FCSTD DOCUMENT  (FreeCAD 0.22R37100 (Git))
Label: composit_stand12_model
License: All rights reserved
LicenseURL: http://en.wikipedia.org/wiki/All_rights_reserved
objects: App::Link×29, App::DocumentObjectGroup×2, PartDesign::CoordinateSystem×1, App::Part×1, Measure::MeasureDistance×1
note: 1 computed .brp shape members not serialized (recipe doc carries the construction recipe); baked Part::Feature solids carry a one-line shape summary decoded from their .brp
EXTERNAL_REF file=composit_stand12.FCStd obj=Local_CS005
EXTERNAL_REF file=composit_stand12.FCStd obj=Body
EXTERNAL_REF file=composit_stand12.FCStd obj=Local_CS004
EXTERNAL_REF file=composit_stand12.FCStd obj=Local_CS006
EXTERNAL_REF file=composit_stand12.FCStd obj=Body002
EXTERNAL_REF file=composit_stand12.FCStd obj=LCS_1
EXTERNAL_REF file=composit_stand12.FCStd obj=Part
EXTERNAL_REF file=composit_stand12.FCStd obj=Local_CS002
EXTERNAL_REF file=composit_stand12.FCStd obj=Local_CS007
EXTERNAL_REF file=composit_stand12.FCStd obj=Body004
EXTERNAL_REF file=composit_stand12.FCStd obj=Local_CS016
EXTERNAL_REF file=composit_stand12.FCStd obj=Local_CS042
EXTERNAL_REF file=composit_stand12.FCStd obj=Body009
EXTERNAL_REF file=composit_stand12.FCStd obj=Local_CS008
EXTERNAL_REF file=composit_stand12.FCStd obj=Local_CS012
EXTERNAL_REF file=composit_stand12.FCStd obj=Body006
EXTERNAL_REF file=composit_stand12.FCStd obj=Local_CS009
EXTERNAL_REF file=composit_stand12.FCStd obj=Local_CS013
EXTERNAL_REF file=composit_stand12.FCStd obj=Body008
EXTERNAL_REF file=composit_stand12.FCStd obj=Local_CS010
EXTERNAL_REF file=composit_stand12.FCStd obj=Local_CS011
EXTERNAL_REF file=composit_stand12.FCStd obj=Local_CS017
EXTERNAL_REF file=composit_stand12.FCStd obj=Local_CS019
EXTERNAL_REF file=composit_stand12.FCStd obj=Body010
EXTERNAL_REF file=composit_stand12.FCStd obj=Local_CS018
EXTERNAL_REF file=composit_stand12.FCStd obj=Body012
EXTERNAL_REF file=../composit_electric_shield.FCStd obj=Local_CS
EXTERNAL_REF file=composit_stand12.FCStd obj=Local_CS020
EXTERNAL_REF file=../composit_electric_shield.FCStd obj=Body
EXTERNAL_REF file=composit_stand12.FCStd obj=Local_CS014
EXTERNAL_REF file=../rails.FCStd obj=LCS_1
EXTERNAL_REF file=../rails.FCStd obj=Part
EXTERNAL_REF file=composit_stand12.FCStd obj=Local_CS015
EXTERNAL_REF file=../basin450x225x125.FCStd obj=Local_CS
EXTERNAL_REF file=composit_stand12.FCStd obj=Local_CS023
EXTERNAL_REF file=../basin450x225x125.FCStd obj=Body
EXTERNAL_REF file=../basin450x225x125.FCStd obj=Local_CS001
EXTERNAL_REF file=../basin450x225x125.FCStd obj=Body001
EXTERNAL_REF file=composit_stand12.FCStd obj=Local_CS024
EXTERNAL_REF file=composit_stand12.FCStd obj=Body015
EXTERNAL_REF file=composit_stand12.FCStd obj=Local_CS025
EXTERNAL_REF file=composit_stand12.FCStd obj=Body016
EXTERNAL_REF file=composit_stand12.FCStd obj=Local_CS027
EXTERNAL_REF file=composit_stand12.FCStd obj=Local_CS028
EXTERNAL_REF file=composit_stand12.FCStd obj=Body018
EXTERNAL_REF file=composit_stand12.FCStd obj=Local_CS029
EXTERNAL_REF file=composit_stand12.FCStd obj=Local_CS030
EXTERNAL_REF file=composit_stand12.FCStd obj=Body019
EXTERNAL_REF file=composit_stand12.FCStd obj=Local_CS001
EXTERNAL_REF file=composit_stand12.FCStd obj=Local_CS003
EXTERNAL_REF file=composit_stand12.FCStd obj=Body005
EXTERNAL_REF file=composit_stand12.FCStd obj=Local_CS031
EXTERNAL_REF file=composit_stand12.FCStd obj=Local_CS032
EXTERNAL_REF file=composit_stand12.FCStd obj=Local_CS033
EXTERNAL_REF file=composit_stand12.FCStd obj=Local_CS034
EXTERNAL_REF file=composit_stand12.FCStd obj=Body022
EXTERNAL_REF file=composit_stand12.FCStd obj=Local_CS035
EXTERNAL_REF file=composit_stand12.FCStd obj=Local_CS036
EXTERNAL_REF file=composit_stand12.FCStd obj=Body023
EXTERNAL_REF file=composit_stand12.FCStd obj=Local_CS040
EXTERNAL_REF file=composit_stand12.FCStd obj=Body025
EXTERNAL_REF file=composit_stand12.FCStd obj=Local_CS039
EXTERNAL_REF file=composit_stand12.FCStd obj=Local_CS041
EXTERNAL_REF file=composit_stand12.FCStd obj=Body026

FEATURE [App::DocumentObjectGroup] Parts
FEATURE [PartDesign::CoordinateSystem] LCS_Origin
  AttacherType = Attacher::AttachEngine3D
  AttachmentOffset = pos=(0,0,0) rot=(0,0,1;3.14159rad)
  AttachmentSupport = -> [XY_Plane]
  MapMode = 5
  Placement = pos=(0,0,0) rot=(0,0,1;3.14159rad)
FEATURE [App::Link] face
  AttachedBy = #Local_CS005
  AttachedTo = Parent Assembly#LCS_Origin
  LinkPlacement = pos=(0,0,0) rot=(0,0,1;3.14159rad)
  LinkedObject = -> <external composit_stand12.FCStd>#Body
  Placement = pos=(0,0,0) rot=(0,0,1;3.14159rad)
  SolverId = Asm4EE
  expr: Placement = LCS_Origin.Placement * AttachmentOffset * composit_stand12#Local_CS005.Placement ^ -1
FEATURE [App::Link] sink
  AttachedBy = #Local_CS004
  AttachedTo = face#Local_CS006
  LinkPlacement = pos=(-3.7e-15,-30,148) rot=(0,0,1;3.14159rad)
  LinkedObject = -> <external composit_stand12.FCStd>#Body002
  Placement = pos=(-3.7e-15,-30,148) rot=(0,0,1;3.14159rad)
  SolverId = Asm4EE
  expr: Placement = face.Placement * composit_stand12#Local_CS006.Placement * AttachmentOffset * composit_stand12#Local_CS004.Placement ^ -1
FEATURE [App::Link] modules
  AttachedBy = #LCS_1
  AttachedTo = face#Local_CS005
  LinkPlacement = pos=(0,0,0) rot=(0,0,1;3.14159rad)
  LinkedObject = -> <external composit_stand12.FCStd>#Part
  Placement = pos=(0,0,0) rot=(0,0,1;3.14159rad)
  SolverId = Asm4EE
  expr: Placement = face.Placement * composit_stand12#Local_CS005.Placement * AttachmentOffset * composit_stand12#LCS_1.Placement ^ -1
FEATURE [App::Link] dropper_fix_composit
  AttachedBy = #Local_CS002
  AttachedTo = face#Local_CS007
  LinkPlacement = pos=(-3.7e-15,-30,1163.4) rot=(0,0,1;3.14159rad)
  LinkedObject = -> <external composit_stand12.FCStd>#Body004
  Placement = pos=(-3.7e-15,-30,1163.4) rot=(0,0,1;3.14159rad)
  SolverId = Asm4EE
  expr: Placement = face.Placement * composit_stand12#Local_CS007.Placement * AttachmentOffset * composit_stand12#Local_CS002.Placement ^ -1
FEATURE [App::Link] pan
  AttachedBy = #Local_CS016
  AttachedTo = face#Local_CS042
  LinkPlacement = pos=(-1.2e-15,-10,10) rot=(0,0,1;3.14159rad)
  LinkedObject = -> <external composit_stand12.FCStd>#Body009
  Placement = pos=(-1.2e-15,-10,10) rot=(0,0,1;3.14159rad)
  SolverId = Asm4EE
  expr: Placement = face.Placement * composit_stand12#Local_CS042.Placement * AttachmentOffset * composit_stand12#Local_CS016.Placement ^ -1
FEATURE [App::Link] bar001
  AttachedBy = #Local_CS008
  AttachedTo = face#Local_CS012
  LinkPlacement = pos=(-3.3e-15,-27,958.5) rot=(0,1,0;1.5708rad)
  LinkedObject = -> <external composit_stand12.FCStd>#Body006
  Placement = pos=(-3.3e-15,-27,958.5) rot=(0,1,0;1.5708rad)
  SolverId = Asm4EE
  expr: Placement = face.Placement * composit_stand12#Local_CS012.Placement * AttachmentOffset * composit_stand12#Local_CS008.Placement ^ -1
FEATURE [App::Link] bar_fix
  AttachedBy = #Local_CS013
  AttachedTo = bar002#Local_CS009
  LinkPlacement = pos=(-444.137,-2,278.5) rot=(0.707107,0,0.707107;3.14159rad)
  LinkedObject = -> <external composit_stand12.FCStd>#Body008
  Placement = pos=(-444.137,-2,278.5) rot=(0.707107,0,0.707107;3.14159rad)
  SolverId = Asm4EE
  expr: Placement = bar002.Placement * composit_stand12#Local_CS009.Placement * AttachmentOffset * composit_stand12#Local_CS013.Placement ^ -1
FEATURE [App::Link] bar_fix001
  AttachedBy = #Local_CS013
  AttachedTo = bar002#Local_CS010
  LinkPlacement = pos=(444.137,-2,278.5) rot=(0.707107,0,-0.707107;3.14159rad)
  LinkedObject = -> <external composit_stand12.FCStd>#Body008
  Placement = pos=(444.137,-2,278.5) rot=(0.707107,0,-0.707107;3.14159rad)
  SolverId = Asm4EE
  expr: Placement = bar002.Placement * composit_stand12#Local_CS010.Placement * AttachmentOffset * composit_stand12#Local_CS013.Placement ^ -1
FEATURE [App::Link] bar_fix002
  AttachedBy = #Local_CS013
  AttachedTo = bar001#Local_CS009
  LinkPlacement = pos=(-444.137,-2,958.5) rot=(0.707107,0,0.707107;3.14159rad)
  LinkedObject = -> <external composit_stand12.FCStd>#Body008
  Placement = pos=(-444.137,-2,958.5) rot=(0.707107,0,0.707107;3.14159rad)
  SolverId = Asm4EE
  expr: Placement = bar001.Placement * composit_stand12#Local_CS009.Placement * AttachmentOffset * composit_stand12#Local_CS013.Placement ^ -1
FEATURE [App::Link] bar_fix003
  AttachedBy = #Local_CS013
  AttachedTo = bar001#Local_CS010
  LinkPlacement = pos=(444.137,-2,958.5) rot=(0.707107,0,-0.707107;3.14159rad)
  LinkedObject = -> <external composit_stand12.FCStd>#Body008
  Placement = pos=(444.137,-2,958.5) rot=(0.707107,0,-0.707107;3.14159rad)
  SolverId = Asm4EE
  expr: Placement = bar001.Placement * composit_stand12#Local_CS010.Placement * AttachmentOffset * composit_stand12#Local_CS013.Placement ^ -1
FEATURE [App::Link] bar002
  AttachedBy = #Local_CS008
  AttachedTo = face#Local_CS011
  LinkPlacement = pos=(-3.3e-15,-27,278.5) rot=(0,1,0;1.5708rad)
  LinkedObject = -> <external composit_stand12.FCStd>#Body006
  Placement = pos=(-3.3e-15,-27,278.5) rot=(0,1,0;1.5708rad)
  SolverId = Asm4EE
  expr: Placement = face.Placement * composit_stand12#Local_CS011.Placement * AttachmentOffset * composit_stand12#Local_CS008.Placement ^ -1
FEATURE [App::Link] cap_outer
  AttachedBy = #Local_CS017
  AttachedTo = face#Local_CS019
  LinkPlacement = pos=(0,0,1163.4) rot=(0,0,1;3.14159rad)
  LinkedObject = -> <external composit_stand12.FCStd>#Body010
  Placement = pos=(0,0,1163.4) rot=(0,0,1;3.14159rad)
  SolverId = Asm4EE
  expr: Placement = face.Placement * composit_stand12#Local_CS019.Placement * AttachmentOffset * composit_stand12#Local_CS017.Placement ^ -1
FEATURE [App::Link] cap_inner
  AttachedBy = #Local_CS018
  AttachedTo = cap_outer#Local_CS017
  LinkPlacement = pos=(0,0,1163.4) rot=(0,0,1;3.14159rad)
  LinkedObject = -> <external composit_stand12.FCStd>#Body012
  Placement = pos=(0,0,1163.4) rot=(0,0,1;3.14159rad)
  SolverId = Asm4EE
  expr: Placement = cap_outer.Placement * composit_stand12#Local_CS017.Placement * AttachmentOffset * composit_stand12#Local_CS018.Placement ^ -1
FEATURE [App::Link] composit_electric_shield_inner
  AttachedBy = #Local_CS
  AttachedTo = face#Local_CS020
  LinkPlacement = pos=(-413.737,-125,930) rot=(-0.57735,0.57735,0.57735;4.18879rad)
  LinkedObject = -> <external ../composit_electric_shield.FCStd>#Body
  Placement = pos=(-413.737,-125,930) rot=(-0.57735,0.57735,0.57735;4.18879rad)
  SolverId = Asm4EE
  expr: Placement = face.Placement * composit_stand12#Local_CS020.Placement * AttachmentOffset * composit_electric_shield#Local_CS.Placement ^ -1
FEATURE [App::Link] rail_Part
  AttachedBy = #LCS_1
  AttachedTo = face#Local_CS014
  LinkPlacement = pos=(-441.137,-4,23) rot=(0.707107,0,0.707107;3.14159rad)
  LinkedObject = -> <external ../rails.FCStd>#Part
  Placement = pos=(-441.137,-4,23) rot=(0.707107,0,0.707107;3.14159rad)
  SolverId = Asm4EE
  expr: Placement = face.Placement * composit_stand12#Local_CS014.Placement * AttachmentOffset * rails#LCS_1.Placement ^ -1
FEATURE [App::Link] rail_Part001
  AttachedBy = #LCS_1
  AttachedTo = face#Local_CS015
  LinkPlacement = pos=(441.137,-4,23) rot=(-0.707107,0,0.707107;3.14159rad)
  LinkedObject = -> <external ../rails.FCStd>#Part
  Placement = pos=(441.137,-4,23) rot=(-0.707107,0,0.707107;3.14159rad)
  SolverId = Asm4EE
  expr: Placement = face.Placement * composit_stand12#Local_CS015.Placement * AttachmentOffset * rails#LCS_1.Placement ^ -1
FEATURE [App::Link] basin450x225x125
  AttachedBy = #Local_CS
  AttachedTo = pan#Local_CS023
  AttachmentOffset = pos=(0,0,0) rot=(0,0,1;3.14159rad)
  LinkPlacement = pos=(-1.59e-14,-130,13) rot=(0,0,1;0rad)
  LinkedObject = -> <external ../basin450x225x125.FCStd>#Body
  Placement = pos=(-1.59e-14,-130,13) rot=(0,0,1;0rad)
  SolverId = Asm4EE
  expr: Placement = pan.Placement * composit_stand12#Local_CS023.Placement * AttachmentOffset * basin450x225x125#Local_CS.Placement ^ -1
FEATURE [App::Link] basin450x225x125_pump_holder
  AttachedBy = #Local_CS001
  AttachedTo = basin450x225x125#Local_CS
  LinkPlacement = pos=(-1.59e-14,-130,13) rot=(0,0,1;0rad)
  LinkedObject = -> <external ../basin450x225x125.FCStd>#Body001
  Placement = pos=(-1.59e-14,-130,13) rot=(0,0,1;0rad)
  SolverId = Asm4EE
  expr: Placement = basin450x225x125.Placement * basin450x225x125#Local_CS.Placement * AttachmentOffset * basin450x225x125#Local_CS001.Placement ^ -1
FEATURE [App::Link] basin_fix
  AttachedBy = #Local_CS024
  AttachedTo = pan#Local_CS016
  LinkPlacement = pos=(-1.2e-15,-10,13) rot=(0,0,1;3.14159rad)
  LinkedObject = -> <external composit_stand12.FCStd>#Body015
  Placement = pos=(-1.2e-15,-10,13) rot=(0,0,1;3.14159rad)
  SolverId = Asm4EE
  expr: Placement = pan.Placement * composit_stand12#Local_CS016.Placement * AttachmentOffset * composit_stand12#Local_CS024.Placement ^ -1
FEATURE [App::Link] door_plexiglass
  AttachedBy = #Local_CS025
  AttachedTo = door_ss#Local_CS026
  LinkPlacement = pos=(3.979e-13,-315.383,250) rot=(0,0,1;3.14159rad)
  LinkedObject = -> <external composit_stand12.FCStd>#Body016
  Placement = pos=(3.979e-13,-315.383,250) rot=(0,0,1;3.14159rad)
  SolverId = Asm4EE
  expr: Placement = door_ss.Placement * composit_stand12#Local_CS026.Placement * AttachmentOffset * composit_stand12#Local_CS025.Placement ^ -1
FEATURE [App::Link] sink_cutout
  AttachedBy = #Local_CS028
  AttachedTo = sink#Local_CS027
  LinkPlacement = pos=(-1.45e-14,-118.451,164.625) rot=(0,0.09276,0.995689;3.14159rad)
  LinkedObject = -> <external composit_stand12.FCStd>#Body018
  Placement = pos=(-1.45e-14,-118.451,164.625) rot=(0,0.09276,0.995689;3.14159rad)
  SolverId = Asm4EE
  expr: Placement = sink.Placement * composit_stand12#Local_CS027.Placement * AttachmentOffset * composit_stand12#Local_CS028.Placement ^ -1
FEATURE [App::Link] sink_jumb
  AttachedBy = #Local_CS030
  AttachedTo = sink#Local_CS029
  LinkPlacement = pos=(-2.56e-14,-216.86,182.409) rot=(1,0,0;6.0974rad)
  LinkedObject = -> <external composit_stand12.FCStd>#Body019
  Placement = pos=(-2.56e-14,-216.86,182.409) rot=(1,0,0;6.0974rad)
  SolverId = Asm4EE
  expr: Placement = sink.Placement * composit_stand12#Local_CS029.Placement * AttachmentOffset * composit_stand12#Local_CS030.Placement ^ -1
FEATURE [App::Link] dropper_fix_PP
  AttachedBy = #Local_CS001
  AttachedTo = dropper_fix_composit#Local_CS003
  LinkPlacement = pos=(-3.7e-15,-30,1166.4) rot=(0,0,1;3.14159rad)
  LinkedObject = -> <external composit_stand12.FCStd>#Body005
  Placement = pos=(-3.7e-15,-30,1166.4) rot=(0,0,1;3.14159rad)
  SolverId = Asm4EE
  expr: Placement = dropper_fix_composit.Placement * composit_stand12#Local_CS003.Placement * AttachmentOffset * composit_stand12#Local_CS001.Placement ^ -1
FEATURE [App::Link] dropper_fix_PP001
  AttachedBy = #Local_CS001
  AttachedTo = dropper_fix_composit#Local_CS031
  LinkPlacement = pos=(-291.934,-135.683,1166.4) rot=(0,0,1;3.83626rad)
  LinkedObject = -> <external composit_stand12.FCStd>#Body005
  Placement = pos=(-291.934,-135.683,1166.4) rot=(0,0,1;3.83626rad)
  SolverId = Asm4EE
  expr: Placement = dropper_fix_composit.Placement * composit_stand12#Local_CS031.Placement * AttachmentOffset * composit_stand12#Local_CS001.Placement ^ -1
FEATURE [App::Link] dropper_fix_PP002
  AttachedBy = #Local_CS001
  AttachedTo = dropper_fix_composit#Local_CS032
  LinkPlacement = pos=(291.934,-135.683,1166.4) rot=(0,0,-1;3.83626rad)
  LinkedObject = -> <external composit_stand12.FCStd>#Body005
  Placement = pos=(291.934,-135.683,1166.4) rot=(0,0,-1;3.83626rad)
  SolverId = Asm4EE
  expr: Placement = dropper_fix_composit.Placement * composit_stand12#Local_CS032.Placement * AttachmentOffset * composit_stand12#Local_CS001.Placement ^ -1
FEATURE [App::Link] door_jumb
  AttachedBy = #Local_CS033
  AttachedTo = dropper_fix_composit#Local_CS034
  LinkPlacement = pos=(-2.73e-14,-223,1163.4) rot=(-1,0,0;3.14159rad)
  LinkedObject = -> <external composit_stand12.FCStd>#Body022
  Placement = pos=(-2.73e-14,-223,1163.4) rot=(-1,0,0;3.14159rad)
  SolverId = Asm4EE
  expr: Placement = dropper_fix_composit.Placement * composit_stand12#Local_CS034.Placement * AttachmentOffset * composit_stand12#Local_CS033.Placement ^ -1
FEATURE [App::Link] pan_face
  AttachedBy = #Local_CS036
  AttachedTo = pan#Local_CS035
  LinkPlacement = pos=(-3.5e-14,-270,10) rot=(0,0.707107,0.707107;3.14159rad)
  LinkedObject = -> <external composit_stand12.FCStd>#Body023
  Placement = pos=(-3.5e-14,-270,10) rot=(0,0.707107,0.707107;3.14159rad)
  SolverId = Asm4EE
  expr: Placement = pan.Placement * composit_stand12#Local_CS035.Placement * AttachmentOffset * composit_stand12#Local_CS036.Placement ^ -1
FEATURE [App::Link] bottom
  AttachedBy = #Local_CS040
  AttachedTo = face#Local_CS005
  LinkPlacement = pos=(0,0,0) rot=(0,0,1;3.14159rad)
  LinkedObject = -> <external composit_stand12.FCStd>#Body025
  Placement = pos=(0,0,0) rot=(0,0,1;3.14159rad)
  SolverId = Asm4EE
  expr: Placement = face.Placement * composit_stand12#Local_CS005.Placement * AttachmentOffset * composit_stand12#Local_CS040.Placement ^ -1
FEATURE [App::Link] bottom_front_connect
  AttachedBy = #Local_CS041
  AttachedTo = bottom#Local_CS039
  LinkPlacement = pos=(-441.137,-3,3) rot=(0,0,1;3.14159rad)
  LinkedObject = -> <external composit_stand12.FCStd>#Body026
  Placement = pos=(-441.137,-3,3) rot=(0,0,1;3.14159rad)
  SolverId = Asm4EE
  expr: Placement = bottom.Placement * composit_stand12#Local_CS039.Placement * AttachmentOffset * composit_stand12#Local_CS041.Placement ^ -1
FEATURE [App::Part] Assembly
  AssemblyType = Part::Link
  Group = -> [LCS_Origin,face,sink,modules,dropper_fix_composit,pan,bar001,bar_fix,bar_fix001,bar_fix002,bar_fix003,bar002,cap_outer,cap_inner,composit_electric_shield_inner,rail_Part,rail_Part001,basin450x225x125,basin450x225x125_pump_holder,basin_fix,door_plexiglass,sink_cutout,sink_jumb,dropper_fix_PP,dropper_fix_PP001,dropper_fix_PP002,door_jumb,pan_face,bottom,bottom_front_connect]
  Origin = -> Origin
  Type = Assembly
FEATURE [Measure::MeasureDistance] Distance  label="Distance: 68,0000 mm"
  Distance = 68
  Position1 = (45,105,68)
  Position2 = (45,105,0)
FEATURE [App::DocumentObjectGroup] Measurements
  Group = -> [Distance]

RESOLVED EXTERNAL PARTS (link-assembly join: the EXTERNAL_REF files above that resolve inside this repo's crawl, each included once):
---- part ../basin450x225x125.FCStd = doc fcstd_e459db04904b (66552 chars; too large to inline — full recipe in that document) ----
---- part ../composit_electric_shield.FCStd = doc fcstd_7e5574ddc39a (52053 chars; too large to inline — full recipe in that document) ----
---- part ../rails.FCStd = doc fcstd_2a261f8851d4 ----
FCSTD DOCUMENT  (FreeCAD 0.22R37100 (Git))
Label: rails
License: All rights reserved
LicenseURL: http://en.wikipedia.org/wiki/All_rights_reserved
objects: Sketcher::SketchObject×4, PartDesign::CoordinateSystem×4, PartDesign::SubShapeBinder×3, Part::Mirroring×2, Part::FeaturePython×2, PartDesign::FeaturePython×2, Part::Extrusion×2, PartDesign::Boolean×2, App::Link×2, App::FeaturePython×2, PartDesign::Body×2, Part::Compound×1, Assembly::JointGroup×1, Assembly::AssemblyObject×1, App::Part×1
note: 24 computed .brp shape members not serialized (recipe doc carries the construction recipe); baked Part::Feature solids carry a one-line shape summary decoded from their .brp

FEATURE [Sketcher::SketchObject] Sketch
  FullyConstrained = true
  sketch-geometry (5):
    g0: LineSegment StartX=0 StartY=0 StartZ=0 EndX=17.25 EndY=0 EndZ=0
    g1: LineSegment StartX=17.25 StartY=12.1 StartZ=0 EndX=13.75 EndY=12.1 EndZ=0
    g2: LineSegment StartX=17.25 StartY=0 StartZ=0 EndX=17.25 EndY=4.16816 EndZ=0
    g3: LineSegment StartX=17.25 StartY=8.83184 StartZ=0 EndX=17.25 EndY=12.1 EndZ=0
    g4: ArcOfCircle CenterX=14 CenterY=6.5 CenterZ=0 NormalX=0 NormalY=0 NormalZ=1 AngleXU=0 Radius=4 StartAngle=5.66082 EndAngle=6.90555
  constraints (16):
    c: Coincident(g-1,g0)
    c: PointOnObject(g0,g-1)
    c: Coincident(g0,g2)
    c: DistanceX(g0) = 17.25
    c: DistanceY(g3) = 12.1
    c: Coincident(g1,g3)
    c: Horizontal(g1)
    c: Vertical(g2)
    c: Vertical(g3)
    c: Coincident(g4,g2)
    c: Coincident(g4,g3)
    c: Vertical(g0,g1)
    c: DistanceX(g1) = 13.75
    c: DistanceY(g4) = 6.5
    c: Radius(g4) = 4
    c: DistanceX(g4) = 14
FEATURE [Part::Mirroring] Part__Mirroring  label="Sketch (Mirror #1)"
  Base = (0,0,0)
  Normal = (1,0,0)
  Source = -> Sketch
FEATURE [Part::FeaturePython] Connect  # WARN: FeaturePython — macro-defined, semantics opaque (R4)
  Objects = -> [Sketch,Part__Mirroring]
  Tolerance = 0
FEATURE [PartDesign::SubShapeBinder] Binder
  BindCopyOnChange = 0
  BindMode = 0
  ClaimChildren = true
  Context = -> Body [Binder.]
  Fuse = false
  MakeFace = true
  OffsetFill = false
  OffsetIntersection = false
  OffsetJoinType = 0
  OffsetOpenResult = false
  PartialLoad = false
  Placement = pos=(0,0,0) rot=(0,0.707107,0.707107;3.14159rad)
  Relative = false
  Support = -> [Connect]
  _Version = 2
FEATURE [PartDesign::FeaturePython] BaseBend  # WARN: FeaturePython — macro-defined, semantics opaque (R4)
  BendSide = 1
  BendSketch = -> Binder
  MidPlane = false
  Reverse = false
  Suppressed = false
  length = 250
  radius = 1
  thickness = 0.8
FEATURE [Sketcher::SketchObject] Sketch001
  FullyConstrained = true
  sketch-geometry (2):
    g0: Circle CenterX=0 CenterY=31.5 CenterZ=0 NormalX=0 NormalY=0 NormalZ=1 AngleXU=0 Radius=2.5
    g1: Circle CenterX=0 CenterY=215 CenterZ=0 NormalX=0 NormalY=0 NormalZ=1 AngleXU=0 Radius=2.5
  constraints (6):
    c: PointOnObject(g0,g-2)
    c: PointOnObject(g1,g-2)
    c: DistanceY(g0) = 31.5
    c: Equal(g0,g1)
    c: Diameter(g0) = 5
    c: DistanceY(g1) = 215
FEATURE [Part::Extrusion] Extrude
  Base = -> Sketch001
  Dir = (0,0,1)
  DirMode = 2
  FaceMakerClass = Part::FaceMakerBullseye
  LengthFwd = 10
  LengthRev = 0
  Solid = true
  Symmetric = false
FEATURE [Part::Compound] Compound
  Links = -> [Extrude]
FEATURE [PartDesign::Boolean] Boolean
  BaseFeature = -> BaseBend
  Group = -> [Compound]
  Refine = true
  Suppressed = false
  Type = 1
  UsePlacement = true
FEATURE [Sketcher::SketchObject] Sketch002
  FullyConstrained = true
  sketch-geometry (2):
    g0: LineSegment StartX=0 StartY=0 StartZ=0 EndX=8.6 EndY=0 EndZ=0
    g1: LineSegment StartX=8.6 StartY=0 StartZ=0 EndX=8.6 EndY=6.3 EndZ=0
  constraints (6):
    c: Coincident(g-1,g0)
    c: PointOnObject(g0,g-1)
    c: Coincident(g0,g1)
    c: Vertical(g1)
    c: DistanceX(g1) = 8.6
    c: DistanceY(g1) = 6.3
FEATURE [Part::Mirroring] Part__Mirroring001  label="Sketch002 (Mirror #2)"
  Base = (0,0,0)
  Normal = (1,0,0)
  Source = -> Sketch002
FEATURE [Part::FeaturePython] Connect001  # WARN: FeaturePython — macro-defined, semantics opaque (R4)
  Objects = -> [Sketch002,Part__Mirroring001]
  Tolerance = 0
FEATURE [PartDesign::SubShapeBinder] Binder001
  BindCopyOnChange = 0
  BindMode = 0
  ClaimChildren = true
  Context = -> Body001 [Binder001.]
  Fuse = false
  MakeFace = true
  OffsetFill = false
  OffsetIntersection = false
  OffsetJoinType = 0
  OffsetOpenResult = false
  PartialLoad = false
  Placement = pos=(0,0,0) rot=(1,0,0;1.5708rad)
  Relative = false
  Support = -> [Connect001]
  _Version = 2
FEATURE [PartDesign::FeaturePython] BaseBend001  # WARN: FeaturePython — macro-defined, semantics opaque (R4)
  BendSide = 1
  BendSketch = -> Binder001
  MidPlane = false
  Reverse = true
  Suppressed = false
  length = 250
  radius = 1
  thickness = 1
FEATURE [Sketcher::SketchObject] Sketch003
  FullyConstrained = true
  sketch-geometry (19):
    g0: ArcOfCircle CenterX=0 CenterY=22 CenterZ=0 NormalX=0 NormalY=0 NormalZ=1 AngleXU=0 Radius=2.25 StartAngle=3.14159 EndAngle=6.28319
    g1: ArcOfCircle CenterX=2e-16 CenterY=27 CenterZ=0 NormalX=0 NormalY=0 NormalZ=1 AngleXU=0 Radius=2.25 StartAngle=0 EndAngle=3.14159
    g2: LineSegment StartX=-2.25 StartY=22 StartZ=0 EndX=-2.25 EndY=27 EndZ=0
    g3: LineSegment StartX=2.25 StartY=22 StartZ=0 EndX=2.25 EndY=27 EndZ=0
    g4: ArcOfCircle CenterX=-2.5 CenterY=41.5 CenterZ=0 NormalX=0 NormalY=0 NormalZ=1 AngleXU=0 Radius=2.25 StartAngle=1.5708 EndAngle=4.71239
    g5: ArcOfCircle CenterX=2.5 CenterY=41.5 CenterZ=0 NormalX=0 NormalY=0 NormalZ=1 AngleXU=0 Radius=2.25 StartAngle=4.71239 EndAngle=7.85398
    g6: LineSegment StartX=-2.5 StartY=43.75 StartZ=0 EndX=2.5 EndY=43.75 EndZ=0
    g7: LineSegment StartX=-2.5 StartY=39.25 StartZ=0 EndX=2.5 EndY=39.25 EndZ=0
    g8: ArcOfCircle CenterX=0 CenterY=193 CenterZ=0 NormalX=0 NormalY=0 NormalZ=1 AngleXU=0 Radius=2.25 StartAngle=3.14159 EndAngle=6.28319
    g9: ArcOfCircle CenterX=1e-16 CenterY=198 CenterZ=0 NormalX=0 NormalY=0 NormalZ=1 AngleXU=0 Radius=2.25 StartAngle=3.5e-15 EndAngle=3.14159
    g10: LineSegment StartX=-2.25 StartY=193 StartZ=0 EndX=-2.25 EndY=198 EndZ=0
    g11: LineSegment StartX=2.25 StartY=193 StartZ=0 EndX=2.25 EndY=198 EndZ=0
    g12: ArcOfCircle CenterX=-2.5 CenterY=212 CenterZ=0 NormalX=0 NormalY=0 NormalZ=1 AngleXU=0 Radius=2.25 StartAngle=1.5708 EndAngle=4.71239
    g13: ArcOfCircle CenterX=2.5 CenterY=212 CenterZ=0 NormalX=0 NormalY=0 NormalZ=1 AngleXU=0 Radius=2.25 StartAngle=4.71239 EndAngle=7.85398
    g14: LineSegment StartX=-2.5 StartY=214.25 StartZ=0 EndX=2.5 EndY=214.25 EndZ=0
    g15: LineSegment StartX=-2.5 StartY=209.75 StartZ=0 EndX=2.5 EndY=209.75 EndZ=0
    g16: Circle CenterX=0 CenterY=221 CenterZ=0 NormalX=0 NormalY=0 NormalZ=1 AngleXU=0 Radius=2.25
    g17: GeomPoint X=-4.75 Y=41.5 Z=0
    g18: GeomPoint X=4.75 Y=41.5 Z=0
  constraints (45):
    c: Tangent(g0,g2) = 1.5708
    c: Tangent(g0,g3) = -1.5708
    c: Tangent(g1,g2) = 1.5708
    c: Tangent(g1,g3) = -1.5708
    c: Equal(g0,g1)
    c: Vertical(g3)
    c: PointOnObject(g0,g-2)
    c: Tangent(g4,g6) = 1.5708
    c: Tangent(g4,g7) = -1.5708
    c: Tangent(g5,g6) = 1.5708
    c: Tangent(g5,g7) = -1.5708
    c: Equal(g4,g5)
    c: Tangent(g8,g10) = 1.5708
    c: Tangent(g8,g11) = -1.5708
    c: Tangent(g9,g10) = 1.5708
    c: Tangent(g9,g11) = -1.5708
    c: Equal(g8,g9)
    c: Vertical(g11)
    c: PointOnObject(g8,g-2)
    c: Tangent(g12,g14) = 1.5708
    c: Tangent(g12,g15) = -1.5708
    c: Tangent(g13,g14) = 1.5708
    c: Tangent(g13,g15) = -1.5708
    c: Equal(g12,g13)
    c: PointOnObject(g16,g-2)
    c: Symmetric(g5,g4,g-2)
    c: Symmetric(g13,g12,g-2)
    c: Equal(g16,g13)
    c: Equal(g13,g9)
    c: Equal(g9,g5)
    c: Equal(g5,g1)
    c: Diameter(g16) = 4.5
    c: PointOnObject(g17,g4)
    c: PointOnObject(g18,g5)
    c: Horizontal(g18,g5)
    c: Horizontal(g5,g17)
    c: DistanceX(g17,g18) = 9.5
    c: Equal(g3,g7)
    c: Equal(g7,g11)
    c: Equal(g11,g15)
    c: DistanceY(g1) = 27
    c: DistanceY(g5) = 41.5
    c: DistanceY(g9) = 198
    c: DistanceY(g13) = 212
    c: DistanceY(g16) = 221
FEATURE [PartDesign::SubShapeBinder] Binder002
  BindCopyOnChange = 0
  BindMode = 0
  ClaimChildren = true
  Fuse = false
  MakeFace = true
  OffsetFill = false
  OffsetIntersection = false
  OffsetJoinType = 0
  OffsetOpenResult = false
  PartialLoad = false
  Relative = false
  Support = -> [Sketch003]
  _Version = 2
FEATURE [Part::Extrusion] Extrude001
  Base = -> Binder002
  Dir = (0,0,1)
  DirMode = 2
  FaceMakerClass = Part::FaceMakerBullseye
  LengthFwd = 10
  LengthRev = 0
  Solid = false
  Symmetric = false
FEATURE [PartDesign::Boolean] Boolean001
  BaseFeature = -> BaseBend001
  Group = -> [Extrude001]
  Refine = true
  Suppressed = false
  Type = 1
  UsePlacement = true
FEATURE [App::Link] Body002
  LinkedObject = -> Body
FEATURE [App::FeaturePython] GroundedJoint  # Assembly grounded joint (typed FeaturePython)
  ObjectToGround = -> Body002
FEATURE [App::Link] Body003
  LinkPlacement = pos=(0,0,12) rot=(0,1,0;3.14159rad)
  LinkedObject = -> Body001
  Placement = pos=(0,0,12) rot=(0,1,0;3.14159rad)
FEATURE [PartDesign::CoordinateSystem] Local_CS
  AttacherType = Attacher::AttachEngine3D
  AttachmentSupport = -> [XY_Plane]
  MapMode = 5
FEATURE [PartDesign::CoordinateSystem] Local_CS001
  AttacherType = Attacher::AttachEngine3D
  AttachmentSupport = -> [XY_Plane001]
  MapMode = 5
FEATURE [PartDesign::Body] Body001
  Group = -> [Binder001,BaseBend001,Boolean001,Local_CS001]
  Origin = -> Origin001
  Tip = -> Boolean001
FEATURE [PartDesign::CoordinateSystem] Local_CS002
  AttacherType = Attacher::AttachEngine3D
  AttachmentOffset = pos=(0,0,12) rot=(0,1,0;3.14159rad)
  AttachmentSupport = -> [XY_Plane]
  MapMode = 5
  Placement = pos=(0,0,12) rot=(0,1,0;3.14159rad)
FEATURE [PartDesign::Body] Body
  Group = -> [Binder,BaseBend,Boolean,Local_CS,Local_CS002]
  Origin = -> Origin
  Tip = -> Boolean
FEATURE [App::FeaturePython] Slider  # Assembly joint (typed FeaturePython)
  Activated = true
  AngleMax = 0
  AngleMin = 0
  Detach1 = false
  Detach2 = false
  Distance = 0
  Distance2 = 0
  EnableAngleMax = false
  EnableAngleMin = false
  EnableLengthMax = false
  EnableLengthMin = false
  EnableLimits = true
  JointType = 3 (Slider)
  LengthMax = 250
  LengthMin = 0
  Offset = (0,0,0)
  Rotation = 0
FEATURE [Assembly::JointGroup] Joints
  Group = -> [GroundedJoint,Slider]
FEATURE [Assembly::AssemblyObject] Assembly  label="rail_Assembly"
  Group = -> [Joints,Body002,GroundedJoint,Body003,Slider]
  Origin = -> Origin002
  Type = Assembly
FEATURE [PartDesign::CoordinateSystem] LCS_1  label="rail_LCS"
  AttacherType = Attacher::AttachEngine3D
  AttachmentSupport = -> [XY_Plane003]
  MapMode = 5
FEATURE [App::Part] Part  label="rail_Part"
  Group = -> [Assembly,LCS_1]
  Origin = -> Origin003
---- part composit_stand12.FCStd = doc fcstd_02e919d733df (291737 chars; too large to inline — full recipe in that document) ----
